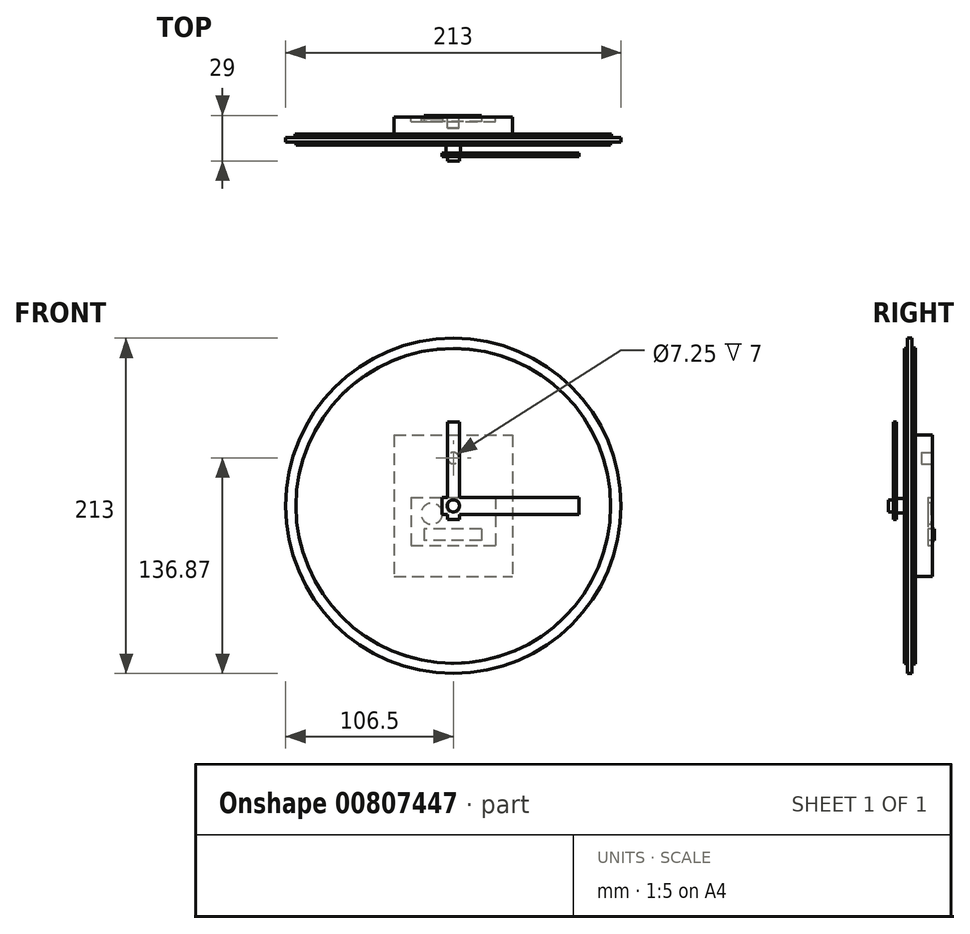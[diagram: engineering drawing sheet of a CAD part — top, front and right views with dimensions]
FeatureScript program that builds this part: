
annotation { "Feature Type Name" : "Feature", "Feature Type Description" : "" }
export const myFeature = defineFeature(function(context is Context, id is Id, definition is map)
    precondition{}
    {
        {
            var Q0;
            Q0=qCreatedBy(makeId("Front.planeOp"),FACE);
            var sketch = newSketch(context, id + "F0", { "sketchPlane" : qUnion([Q0])});
            skCircle(sketch, "E0", {"center": v(0, 0) * mm, "radius": 106.5 * mm});
            skSolve(sketch);
        }
        {
            var Q0;
            Q0=makeQuery(id+"F0.imprint","IMPRINT",FACE,{"disambiguationData":[TD([[makeQuery(id+"F0.imprint","IMPRINT",EDGE,{"derivedFrom":sQuery(id+"F0.wireOp",EDGE,"E0")}),1.0]])]});
            extrude(context, id + "F1", {"entities" : qUnion([Q0]), "depth" : 5 * mm, "offsetDistance" : 25 * mm});
        }
        {
            var Q0;
            Q0=makeQuery(id+"F1.opExtrude","CAP_FACE",FACE,{"disambiguationData":[OSD([sQuery(id+"F0.wireOp",EDGE,"E0")])],"isStart":false});
            var sketch = newSketch(context, id + "F2", { "sketchPlane" : qUnion([Q0])});
            skCircle(sketch, "E1", {"center": v(0, 0) * mm, "radius": 4.6 * mm});
            skSolve(sketch);
        }
        {
            var Q0;
            Q0 = qSketchRegion(id + "F2", true);
            extrude(context, id + "F3", {"entities" : qUnion([Q0]), "operationType" : NewBodyOperationType.ADD, "depth" : 5 * mm, "offsetDistance" : 25 * mm});
        }
        {
            var Q0;
            Q0=makeQuery(id+"F3.opExtrude","CAP_FACE",FACE,{"disambiguationData":[OSD([sQuery(id+"F2.wireOp",EDGE,"E1")])],"isStart":false});
            var sketch = newSketch(context, id + "F4", { "sketchPlane" : qUnion([Q0])});
            skLineSegment(sketch, "E2.bottom", {"start": v(-7.04, 5.43) * mm, "end": v(79.85, 5.43) * mm});
            skLineSegment(sketch, "E2.top", {"start": v(-7.04, -5.43) * mm, "end": v(79.85, -5.43) * mm});
            skLineSegment(sketch, "E2.left", {"start": v(-7.04, 5.43) * mm, "end": v(-7.04, -5.43) * mm});
            skLineSegment(sketch, "E2.right", {"start": v(79.85, 5.43) * mm, "end": v(79.85, -5.43) * mm});
            skLineSegment(sketch, "E3.bottom", {"start": v(-3.82, -8.65) * mm, "end": v(3.82, -8.65) * mm});
            skLineSegment(sketch, "E3.top", {"start": v(-3.82, 53.3) * mm, "end": v(3.82, 53.3) * mm});
            skLineSegment(sketch, "E3.left", {"start": v(-3.82, -8.65) * mm, "end": v(-3.82, 53.3) * mm});
            skLineSegment(sketch, "E3.right", {"start": v(3.82, -8.65) * mm, "end": v(3.82, 53.3) * mm});
            skSolve(sketch);
        }
        {
            var Q0;
            {var subQ5=sQuery(id+"F4.wireOp",EDGE,"E2.right");Q0=makeQuery(id+"F4.imprint","IMPRINT",FACE,{"disambiguationData":[TD([[makeQuery(id+"F4.imprint","IMPRINT",EDGE,{"derivedFrom":subQ5}),-1.0]])]});}
            var Q1;
            Q1 = qSketchRegion(id + "F4", true);
            extrude(context, id + "F5", {"entities" : qUnion([Q0, Q1]), "operationType" : NewBodyOperationType.ADD, "depth" : 2 * mm, "offsetDistance" : 25 * mm});
        }
        {
            var Q0;
            Q0=makeQuery(id+"F1.opExtrude","CAP_FACE",FACE,{"disambiguationData":[OSD([sQuery(id+"F0.wireOp",EDGE,"E0")])],"isStart":false});
            var sketch = newSketch(context, id + "F6", { "sketchPlane" : qUnion([Q0])});
            skCircle(sketch, "E4", {"center": v(0, 0) * mm, "radius": 99.94 * mm});
            skSolve(sketch);
        }
        {
            var Q0;
            Q0=makeQuery(id+"F6.imprint","IMPRINT",FACE,{"disambiguationData":[TD([[makeQuery(id+"F6.imprint","IMPRINT",EDGE,{"derivedFrom":sQuery(id+"F6.wireOp",EDGE,"E4")}),-1.0]])]});
            extrude(context, id + "F7", {"entities" : qUnion([Q0]), "operationType" : NewBodyOperationType.REMOVE, "oppositeDirection" : true, "depth" : 2 * mm, "offsetDistance" : 25 * mm});
        }
        {
            var Q0;
            Q0=makeQuery(id+"F1.opExtrude","CAP_FACE",FACE,{"disambiguationData":[OSD([sQuery(id+"F0.wireOp",EDGE,"E0")])],"isStart":true});
            var sketch = newSketch(context, id + "F8", { "sketchPlane" : qUnion([Q0])});
            skLineSegment(sketch, "E5.bottom", {"start": v(37.61, 44.85) * mm, "end": v(-37.61, 44.85) * mm});
            skLineSegment(sketch, "E5.top", {"start": v(37.61, -44.85) * mm, "end": v(-37.61, -44.85) * mm});
            skLineSegment(sketch, "E5.left", {"start": v(37.61, 44.85) * mm, "end": v(37.61, -44.85) * mm});
            skLineSegment(sketch, "E5.right", {"start": v(-37.61, 44.85) * mm, "end": v(-37.61, -44.85) * mm});
            skPoint(sketch, "E5.middle", {"position": v(0, 0) * mm});
            skSolve(sketch);
        }
        {
            var Q0;
            Q0=makeQuery(id+"F8.imprint","IMPRINT",FACE,{"disambiguationData":[TD([[makeQuery(id+"F8.imprint","IMPRINT",EDGE,{"derivedFrom":sQuery(id+"F8.wireOp",EDGE,"E5.bottom")}),1.0]])]});
            extrude(context, id + "F9", {"entities" : qUnion([Q0]), "operationType" : NewBodyOperationType.ADD, "depth" : 13 * mm, "offsetDistance" : 25 * mm});
        }
        {
            var Q0;
            Q0=makeQuery(id+"F9.opExtrude","CAP_FACE",FACE,{"disambiguationData":[OSD([sQuery(id+"F8.wireOp",EDGE,"E5.bottom"),sQuery(id+"F8.wireOp",EDGE,"E5.top"),sQuery(id+"F8.wireOp",EDGE,"E5.left"),sQuery(id+"F8.wireOp",EDGE,"E5.right")])],"isStart":false});
            var sketch = newSketch(context, id + "F10", { "sketchPlane" : qUnion([Q0])});
            skLineSegment(sketch, "E6.bottom", {"start": v(26.75, 5.43) * mm, "end": v(-26.75, 5.43) * mm});
            skLineSegment(sketch, "E6.top", {"start": v(26.75, -25.14) * mm, "end": v(-26.75, -25.14) * mm});
            skLineSegment(sketch, "E6.left", {"start": v(26.75, 5.43) * mm, "end": v(26.75, -25.14) * mm});
            skLineSegment(sketch, "E6.right", {"start": v(-26.75, 5.43) * mm, "end": v(-26.75, -25.14) * mm});
            skPoint(sketch, "E6.middle", {"position": v(0, -9.86) * mm});
            skSolve(sketch);
        }
        {
            var Q0;
            Q0=makeQuery(id+"F10.imprint","IMPRINT",FACE,{"disambiguationData":[TD([[makeQuery(id+"F10.imprint","IMPRINT",EDGE,{"derivedFrom":sQuery(id+"F10.wireOp",EDGE,"E6.bottom")}),1.0]])]});
            extrude(context, id + "F11", {"entities" : qUnion([Q0]), "operationType" : NewBodyOperationType.REMOVE, "oppositeDirection" : true, "depth" : 3 * mm, "offsetDistance" : 25 * mm});
        }
        {
            var Q0;
            Q0=makeQuery(id+"F11.boolean.opBoolean","COPY",FACE,{"derivedFrom":makeQuery(id+"F11.opExtrude","CAP_FACE",FACE,{"disambiguationData":[OSD([sQuery(id+"F10.wireOp",EDGE,"E6.bottom"),sQuery(id+"F10.wireOp",EDGE,"E6.top"),sQuery(id+"F10.wireOp",EDGE,"E6.left"),sQuery(id+"F10.wireOp",EDGE,"E6.right")])],"isStart":false})});
            var sketch = newSketch(context, id + "F12", { "sketchPlane" : qUnion([Q0])});
            skCircle(sketch, "E7", {"center": v(13.72, -5.03) * mm, "radius": 6.72 * mm});
            skSolve(sketch);
        }
        {
            var Q0;
            Q0 = qSketchRegion(id + "F12", true);
            extrude(context, id + "F13", {"entities" : qUnion([Q0]), "operationType" : NewBodyOperationType.ADD, "depth" : 2 * mm, "offsetDistance" : 25 * mm});
        }
        {
            var Q0;
            Q0=makeQuery(id+"F9.opExtrude","CAP_FACE",FACE,{"disambiguationData":[OSD([sQuery(id+"F8.wireOp",EDGE,"E5.bottom"),sQuery(id+"F8.wireOp",EDGE,"E5.top"),sQuery(id+"F8.wireOp",EDGE,"E5.left"),sQuery(id+"F8.wireOp",EDGE,"E5.right")])],"isStart":false});
            var sketch = newSketch(context, id + "F14", { "sketchPlane" : qUnion([Q0])});
            skCircle(sketch, "E8", {"center": v(0, 30.37) * mm, "radius": 3.63 * mm});
            skSolve(sketch);
        }
        {
            var Q0;
            Q0 = qSketchRegion(id + "F14", true);
            extrude(context, id + "F15", {"entities" : qUnion([Q0]), "operationType" : NewBodyOperationType.REMOVE, "oppositeDirection" : true, "depth" : 7 * mm, "offsetDistance" : 25 * mm});
        }
        {
            var Q0;
            Q0=makeQuery(id+"F11.boolean.opBoolean","COPY",FACE,{"derivedFrom":makeQuery(id+"F11.opExtrude","CAP_FACE",FACE,{"disambiguationData":[OSD([sQuery(id+"F10.wireOp",EDGE,"E6.bottom"),sQuery(id+"F10.wireOp",EDGE,"E6.top"),sQuery(id+"F10.wireOp",EDGE,"E6.left"),sQuery(id+"F10.wireOp",EDGE,"E6.right")])],"isStart":false})});
            var sketch = newSketch(context, id + "F16", { "sketchPlane" : qUnion([Q0])});
            skLineSegment(sketch, "E9.bottom", {"start": v(-17.9, -14.68) * mm, "end": v(18.7, -14.68) * mm});
            skLineSegment(sketch, "E9.top", {"start": v(-17.9, -21.92) * mm, "end": v(18.7, -21.92) * mm});
            skLineSegment(sketch, "E9.left", {"start": v(-17.9, -14.68) * mm, "end": v(-17.9, -21.92) * mm});
            skLineSegment(sketch, "E9.right", {"start": v(18.7, -14.68) * mm, "end": v(18.7, -21.92) * mm});
            skSolve(sketch);
        }
        {
            var Q0;
            Q0=makeQuery(id+"F16.imprint","IMPRINT",FACE,{"disambiguationData":[TD([[makeQuery(id+"F16.imprint","IMPRINT",EDGE,{"derivedFrom":sQuery(id+"F16.wireOp",EDGE,"E9.bottom")}),-1.0]])]});
            extrude(context, id + "F17", {"entities" : qUnion([Q0]), "operationType" : NewBodyOperationType.ADD, "depth" : 4 * mm, "offsetDistance" : 25 * mm});
        }
        {
            var Q0;
            Q0=makeQuery(id+"F5.opExtrude","CAP_FACE",FACE,{"disambiguationData":[OSD([sQuery(id+"F4.wireOp",EDGE,"E2.bottom"),sQuery(id+"F4.wireOp",EDGE,"E2.top"),sQuery(id+"F4.wireOp",EDGE,"E2.left"),sQuery(id+"F4.wireOp",EDGE,"E2.right"),sQuery(id+"F4.wireOp",EDGE,"E3.bottom"),sQuery(id+"F4.wireOp",EDGE,"E3.top"),sQuery(id+"F4.wireOp",EDGE,"E3.left"),sQuery(id+"F4.wireOp",EDGE,"E3.right")])],"isStart":false});
            var sketch = newSketch(context, id + "F18", { "sketchPlane" : qUnion([Q0])});
            skCircle(sketch, "E10", {"center": v(0, 0) * mm, "radius": 3.82 * mm});
            skSolve(sketch);
        }
        {
            var Q0;
            Q0 = qSketchRegion(id + "F18", true);
            extrude(context, id + "F19", {"entities" : qUnion([Q0]), "operationType" : NewBodyOperationType.ADD, "depth" : 3 * mm, "offsetDistance" : 25 * mm});
        }
        {
            var Q0;
            Q0=makeQuery(id+"F1.opExtrude","CAP_FACE",FACE,{"disambiguationData":[OSD([sQuery(id+"F0.wireOp",EDGE,"E0")])],"isStart":true});
            var sketch = newSketch(context, id + "F20", { "sketchPlane" : qUnion([Q0])});
            skCircle(sketch, "E11", {"center": v(0, 0) * mm, "radius": 100.37 * mm});
            skSolve(sketch);
        }
        {
            var Q0;
            Q0=makeQuery(id+"F20.imprint","IMPRINT",FACE,{"disambiguationData":[TD([[makeQuery(id+"F20.imprint","IMPRINT",EDGE,{"derivedFrom":sQuery(id+"F20.wireOp",EDGE,"E11")}),1.0]])]});
            extrude(context, id + "F21", {"entities" : qUnion([Q0]), "operationType" : NewBodyOperationType.ADD, "depth" : 2 * mm, "offsetDistance" : 25 * mm});
        }
    });
